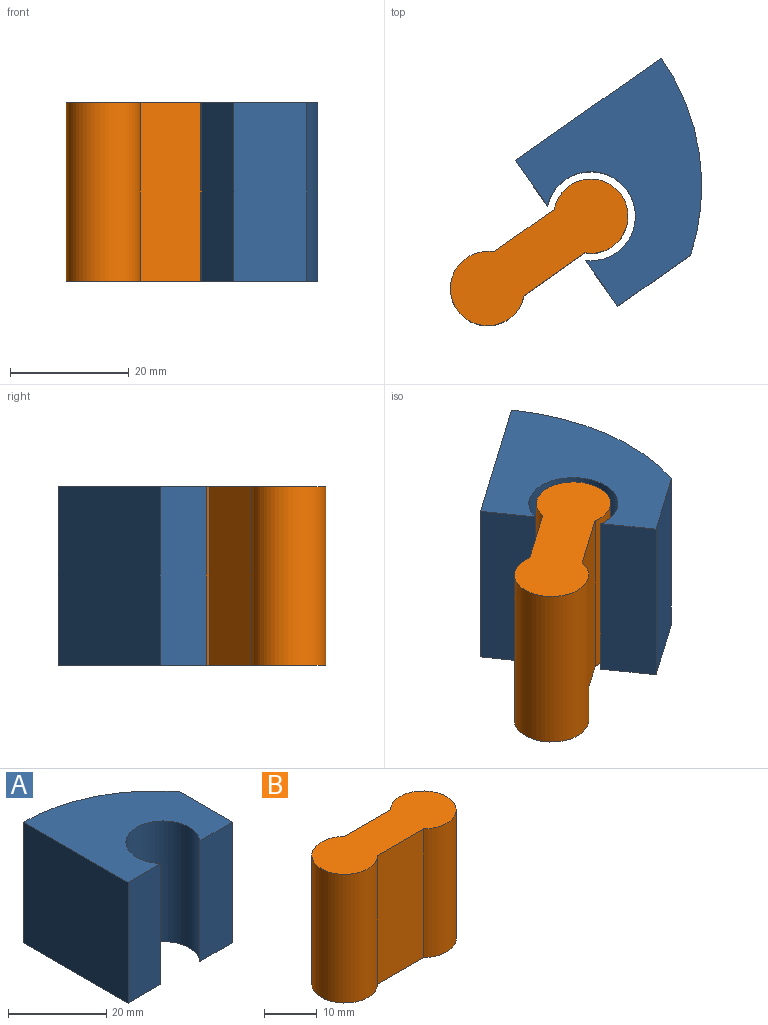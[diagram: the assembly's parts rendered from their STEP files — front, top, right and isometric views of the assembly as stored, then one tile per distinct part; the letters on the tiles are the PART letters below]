
ASSEMBLY  parts=2 mates=1
PART A: 8 faces, bbox 30x30x30 mm
  f0: plane 30x9.41mm, normal (0,-1,0), area 282.3mm2, adj f2,f3,f6,f7
  f1: plane 30x9.41mm, normal (0,-1,0), area 282.3mm2, adj f2,f4,f6,f7
  f2: plane 30x30mm, normal (0,0,1), area 607.1mm2, adj f0,f1,f3,f4,f5,f7
  f3: plane 30x30mm, normal (-1,0,0), area 900mm2, adj f0,f2,f5,f6
  f4: plane 30x15mm, normal (1,0,0), area 450mm2, adj f1,f2,f5,f6
  f5: cylinder r=37.5mm len=30mm, axis (0,0,-1), area 1043.2mm2, adj f2,f3,f4,f6
  f6: plane 30x30mm, normal (0,0,-1), area 607.1mm2, adj f0,f1,f3,f4,f5,f7
  f7: cylinder r=7.5mm len=30mm, axis (0,0,1), area 1035.2mm2, adj f0,f1,f2,f6
PART B: 6 faces, bbox 33.7x12.5x30 mm
  f0: plane 30x12.5mm, normal (0,1,0), area 375mm2, adj f1,f3,f4,f5
  f1: cylinder r=6.25mm len=30mm, axis (0,0,1), area 878.6mm2, adj f0,f2,f4,f5
  f2: plane 30x12.5mm, normal (0,-1,0), area 375mm2, adj f1,f3,f4,f5
  f3: cylinder r=6.25mm len=30mm, axis (0,0,1), area 878.6mm2, adj f0,f2,f4,f5
  f4: plane 33.72x12.5mm, normal (0,0,-1), area 334mm2, adj f0,f1,f2,f3
  f5: plane 33.72x12.5mm, normal (0,0,1), area 334mm2, adj f0,f1,f2,f3
PLACE A rot(axis=(0,0,-1),55deg) t=(71.99,73.71,-15.42)mm
PLACE B rot(axis=(0,0,1),35deg) t=(78.03,52,14.58)mm
MATE fastened B.f3 <-> A.f7  axis (0,0,1) through (84.69,64.29,14.58)mm
